# Revit family: Reece_Basin_LAUFEN_Kartell_Wall or Above Counter Basin_1200 mm
name_source: partatom
category: Plumbing Fixtures
revit_build: Autodesk Revit 2018 (Build: 20180329_1100(x64)
units: mm (PartAtom-declared; Revit-internal decimal feet)

## family parameters
Always vertical = Yes
Cut with Voids When Loaded = Yes
Part Type = Normal
Room Calculation Point = Yes
Round Connector Dimension = Use Diameter
Shared = Yes
Work Plane-Based = Yes

## types (1)
- Left Hand Bowl_1 Taphole_SaphirKeramik_White
    Default Elevation = 0 mm  [stored 0 ft]
    Description = LAUFEN Kartell Wall/Counter Left Hand Basin 1 Tap Hole 1200x460 with Fixing Bolts White
    Disclaimer = THIS FILE IS THE PROPERTY OF THE REECE GROUP. IT MAY NOT BE REPRODUCED, REVERSE-ENGINEERED OR MODIFIED. ANY REPUBLICATION, TRANSMISSION OR DISTRIBUTION FOR THE PURPOSE OF COMMERCIALLY EXPLOITING THE FILES IS PROHIBITED.
    Keynote = Product #1810930, Reece_Basin_LAUFEN_Kartell_Wall or Above Counter Basin_1200 mm - Left Hand Bowl_1 Taphole_SaphirKeramik_White
    Manufacturer = LAUFEN
    Model = Kartell
    Reece_Basin_Outlet = 40 mm  [stored 0.131234 ft]
    Reece_Basin_Supply Diameter 1 = 0 mm  [stored 0 ft]
    Reece_Detail_Disclaimer = THIS FILE IS THE PROPERTY OF THE REECE GROUP. IT MAY NOT BE REPRODUCED, REVERSE-ENGINEERED OR MODIFIED. ANY REPUBLICATION, TRANSMISSION OR DISTRIBUTION FOR THE PURPOSE OF COMMERCIALLY EXPLOITING THE FILES IS PROHIBITED.
    Reece_Height_From_Level = 900 mm  [stored 2.95276 ft]
    Reece_Material_Main = Reece_SaphirKeramik_White
    Reece_Overall_Capacity = 6.6 L
    Reece_Overall_Height = 150 mm
    Reece_Overall_Length = 1200 mm  [stored 3.93701 ft]
    Reece_Overall_Width = 460 mm
    Reece_Product_Brand = LAUFEN
    Reece_Product_Description = LAUFEN Kartell Wall/Counter Left Hand Basin 1 Taphole 1200x460 with Fixing Bolts White
    Reece_Product_Mount = Wall Mounted
    Reece_Product_Number = 1810930
    Reece_Product_Sub Brand = Kartell
    Reece_Product_Type = Basin
    Reece_Product_Web Page = https://www.reece.com.au
    Type Comments = Basin
    URL = https://www.reece.com.au

note: [stored X ft] marks values corroborated as IEEE doubles in the binary element streams (Revit-internal decimal feet)

## geometry (parser evidence)
native form markers: Sweep x3
no freeform markers — native parametric forms only
